# Revit family: Plymold-Communal_Tables-Bar_Table
name_source: partatom
category: Furniture
units: mm (PartAtom-declared; Revit-internal decimal feet)

## family parameters
Always vertical = Yes
Cut with Voids When Loaded = No
OmniClass Number = 23.40.20.00
OmniClass Title = General Furniture and Specialties
Render Appearance Source = Family Geometry
Room Calculation Point = No
Shared = No
Work Plane-Based = No

## types (4) — shared parameters
Assembly Code = E2020200
Default Elevation = 0"
Depth = 30"
FRAME MATERIAL = PLY - Onyx Black Powdercoat
GLIDES MATERIAL = PLY - Plastic Black
Height = 42"
Keynote = 12500
Manufacturer = Plymold Inc.
POWER MATERIAL = PLY - Plastic Black
Product Documentation Link = https://plymold.com
Revit File Built By = https://servex-us.com
Sustainability = https://plymold.com
TOP MATERIAL = PLY - Wood Mahogany
TRAY MATERIAL = PLY - Onyx Black Powdercoat
Type Comments = Communal Tables
URL = https://plymold.com

## per-type parameters (varying)
| type | Description | Dist Power | Dur A Edge | EDGE MATERIAL | Solid Beech Table | Width |
| 30072TPDH42 | Hero Base - Thin Profile Dur-A-Edge® Table Tops - 72"W x 30"D x 42"H | 9/16" | Yes | PLY - Plastic Black | No | 72" |
| 30096TPDH42 | Hero Base - Thin Profile Dur-A-Edge® Table Tops  - 96"W x 30"D x 42"H | 9/16" | Yes | PLY - Plastic Black | No | 96" |
| 30072SWH42 | Hero Base - Solid Beech Wide Edge Grain Table Tops - 72"W x 30"D x 42"H | 0" | No | PLY - Wood Mahogany | Yes | 72" |
| 30096SWH42 | Hero Base - Solid Beech Wide Edge Grain Table Tops - 96"W x 30"D x 42"H | 0" | No | PLY - Wood Mahogany | Yes | 96" |

note: column(s) folded — value = type name in every type: Model

## geometry (parser evidence)
native form markers: Sweep x10
no freeform markers — native parametric forms only
